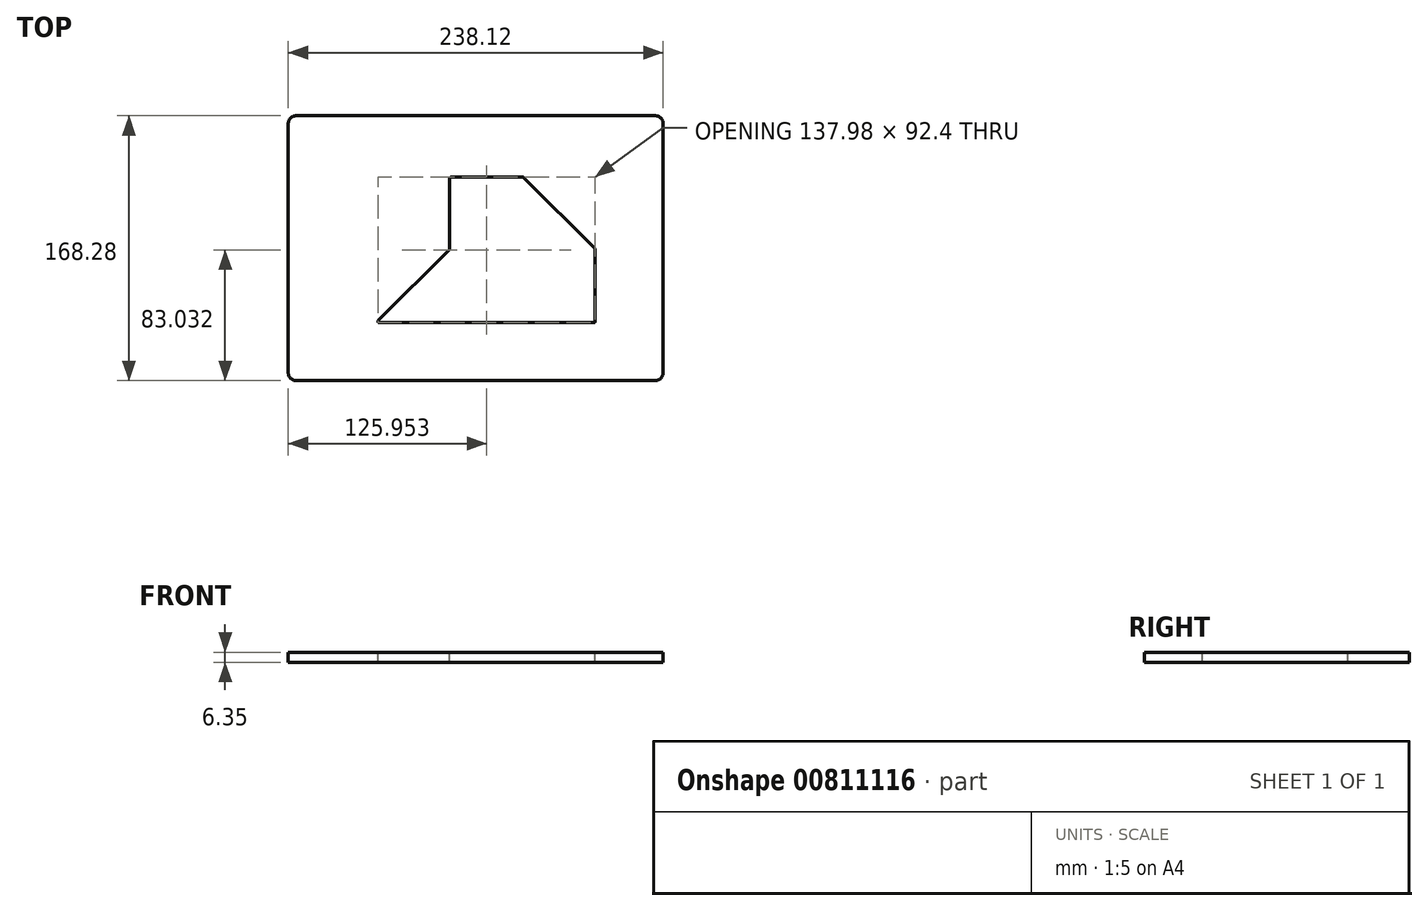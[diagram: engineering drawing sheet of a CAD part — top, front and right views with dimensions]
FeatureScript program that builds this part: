
annotation { "Feature Type Name" : "Feature", "Feature Type Description" : "" }
export const myFeature = defineFeature(function(context is Context, id is Id, definition is map)
    precondition{}
    {
        {
            var Q0;
            Q0=qCreatedBy(makeId("Top.planeOp"),FACE);
            var sketch = newSketch(context, id + "F0", { "sketchPlane" : qUnion([Q0])});
            skLineSegment(sketch, "E0.bottom", {"start": v(-113.98, 84.14) * mm, "end": v(113.98, 84.14) * mm});
            skLineSegment(sketch, "E0.top", {"start": v(-113.98, -84.14) * mm, "end": v(113.98, -84.14) * mm});
            skLineSegment(sketch, "E0.left", {"start": v(-119.06, 79.06) * mm, "end": v(-119.06, -79.06) * mm});
            skLineSegment(sketch, "E0.right", {"start": v(119.06, 79.06) * mm, "end": v(119.06, -79.06) * mm});
            skPoint(sketch, "E0.middle", {"position": v(0, 0) * mm});
            skPoint(sketch, "E1.visualSharp", {"position": v(-119.06, -84.14) * mm});
            skArc(sketch, "E1.filletArc", {"start": v(-119.06, -79.06) * mm, "mid": v(-117.57, -82.65) * mm, "end": v(-113.98, -84.14) * mm});
            skPoint(sketch, "E2.visualSharp", {"position": v(-119.06, 84.14) * mm});
            skArc(sketch, "E2.filletArc", {"start": v(-113.98, 84.14) * mm, "mid": v(-117.57, 82.65) * mm, "end": v(-119.06, 79.06) * mm});
            skPoint(sketch, "E3.visualSharp", {"position": v(119.06, 84.14) * mm});
            skArc(sketch, "E3.filletArc", {"start": v(119.06, 79.06) * mm, "mid": v(117.57, 82.65) * mm, "end": v(113.98, 84.14) * mm});
            skPoint(sketch, "E4.visualSharp", {"position": v(119.06, -84.14) * mm});
            skArc(sketch, "E4.filletArc", {"start": v(113.98, -84.14) * mm, "mid": v(117.57, -82.65) * mm, "end": v(119.06, -79.06) * mm});
            skSolve(sketch);
        }
        {
            var Q0;
            Q0 = qSketchRegion(id + "F0", true);
            extrude(context, id + "F1", {"entities" : qUnion([Q0]), "depth" : 6.35 * mm, "offsetDistance" : 25.4 * mm});
        }
        {
            var Q0;
            Q0=makeQuery(id+"F1.opExtrude","CAP_FACE",FACE,{"disambiguationData":[OSD([sQuery(id+"F0.wireOp",EDGE,"E0.bottom"),sQuery(id+"F0.wireOp",EDGE,"E0.top"),sQuery(id+"F0.wireOp",EDGE,"E0.left"),sQuery(id+"F0.wireOp",EDGE,"E0.right"),sQuery(id+"F0.wireOp",EDGE,"E1.filletArc"),sQuery(id+"F0.wireOp",EDGE,"E2.filletArc"),sQuery(id+"F0.wireOp",EDGE,"E3.filletArc"),sQuery(id+"F0.wireOp",EDGE,"E4.filletArc")])],"isStart":false});
            var sketch = newSketch(context, id + "F2", { "sketchPlane" : qUnion([Q0])});
            skLineSegment(sketch, "E5", {"start": v(-60.15, -46.04) * mm, "end": v(74.61, -46.04) * mm});
            skLineSegment(sketch, "E6", {"start": v(74.61, -46.04) * mm, "end": v(74.61, -1.08) * mm});
            skLineSegment(sketch, "E7", {"start": v(74.61, -1.08) * mm, "end": v(29.71, 43.82) * mm});
            skLineSegment(sketch, "E8", {"start": v(29.71, 43.82) * mm, "end": v(-15.25, 43.82) * mm});
            skLineSegment(sketch, "E9", {"start": v(-15.25, 43.82) * mm, "end": v(-15.25, -1.14) * mm});
            skLineSegment(sketch, "E10", {"start": v(-15.25, -1.14) * mm, "end": v(-60.15, -46.04) * mm});
            skSolve(sketch);
        }
        {
            var Q0;
            Q0 = qSketchRegion(id + "F2", true);
            extrude(context, id + "F3", {"entities" : qUnion([Q0]), "operationType" : NewBodyOperationType.REMOVE, "oppositeDirection" : true, "depth" : 25.4 * mm, "offsetDistance" : 25.4 * mm});
        }
        {
            var Q0;
            Q0=makeQuery(id+"F1.opExtrude","CAP_FACE",FACE,{"disambiguationData":[OSD([sQuery(id+"F0.wireOp",EDGE,"E0.bottom"),sQuery(id+"F0.wireOp",EDGE,"E0.top"),sQuery(id+"F0.wireOp",EDGE,"E0.left"),sQuery(id+"F0.wireOp",EDGE,"E0.right"),sQuery(id+"F0.wireOp",EDGE,"E1.filletArc"),sQuery(id+"F0.wireOp",EDGE,"E2.filletArc"),sQuery(id+"F0.wireOp",EDGE,"E3.filletArc"),sQuery(id+"F0.wireOp",EDGE,"E4.filletArc")])],"isStart":false});
            var sketch = newSketch(context, id + "F4", { "sketchPlane" : qUnion([Q0])});
            skLineSegment(sketch, "E11.0", {"start": v(75.65, -0.32) * mm, "end": v(30.47, 44.86) * mm});
            skLineSegment(sketch, "E11.1", {"start": v(-16.52, 44.3) * mm, "end": v(-16.52, -0.28) * mm});
            skLineSegment(sketch, "E11.2", {"start": v(-16.75, -0.84) * mm, "end": v(-61.87, -45.96) * mm});
            skLineSegment(sketch, "E11.3", {"start": v(29.91, 45.1) * mm, "end": v(-15.73, 45.1) * mm});
            skLineSegment(sketch, "E11.4", {"start": v(-61.31, -47.3) * mm, "end": v(75.1, -47.3) * mm});
            skLineSegment(sketch, "E11.5", {"start": v(75.88, -46.52) * mm, "end": v(75.88, -0.88) * mm});
            skPoint(sketch, "E12.visualSharp", {"position": v(30.24, 45.1) * mm});
            skArc(sketch, "E12.filletArc", {"start": v(30.47, 44.86) * mm, "mid": v(30.21, 45.03) * mm, "end": v(29.91, 45.1) * mm});
            skPoint(sketch, "E13.visualSharp", {"position": v(-16.52, 45.1) * mm});
            skArc(sketch, "E13.filletArc", {"start": v(-15.73, 45.1) * mm, "mid": v(-16.29, 44.86) * mm, "end": v(-16.52, 44.3) * mm});
            skPoint(sketch, "E14.visualSharp", {"position": v(75.88, -0.55) * mm});
            skArc(sketch, "E14.filletArc", {"start": v(75.88, -0.88) * mm, "mid": v(75.82, -0.58) * mm, "end": v(75.65, -0.32) * mm});
            skPoint(sketch, "E15.visualSharp", {"position": v(-16.52, -0.61) * mm});
            skArc(sketch, "E15.filletArc", {"start": v(-16.75, -0.84) * mm, "mid": v(-16.58, -0.59) * mm, "end": v(-16.52, -0.28) * mm});
            skPoint(sketch, "E16.visualSharp", {"position": v(75.88, -47.3) * mm});
            skArc(sketch, "E16.filletArc", {"start": v(75.1, -47.3) * mm, "mid": v(75.65, -47.08) * mm, "end": v(75.88, -46.52) * mm});
            skPoint(sketch, "E17.visualSharp", {"position": v(-63.21, -47.3) * mm});
            skArc(sketch, "E17.filletArc", {"start": v(-61.87, -45.96) * mm, "mid": v(-62.04, -46.82) * mm, "end": v(-61.31, -47.3) * mm});
            skSolve(sketch);
        }
        {
            var Q0;
            Q0 = qSketchRegion(id + "F4", true);
            extrude(context, id + "F5", {"entities" : qUnion([Q0]), "operationType" : NewBodyOperationType.REMOVE, "oppositeDirection" : true, "depth" : 25.4 * mm, "offsetDistance" : 25.4 * mm});
        }
    });
